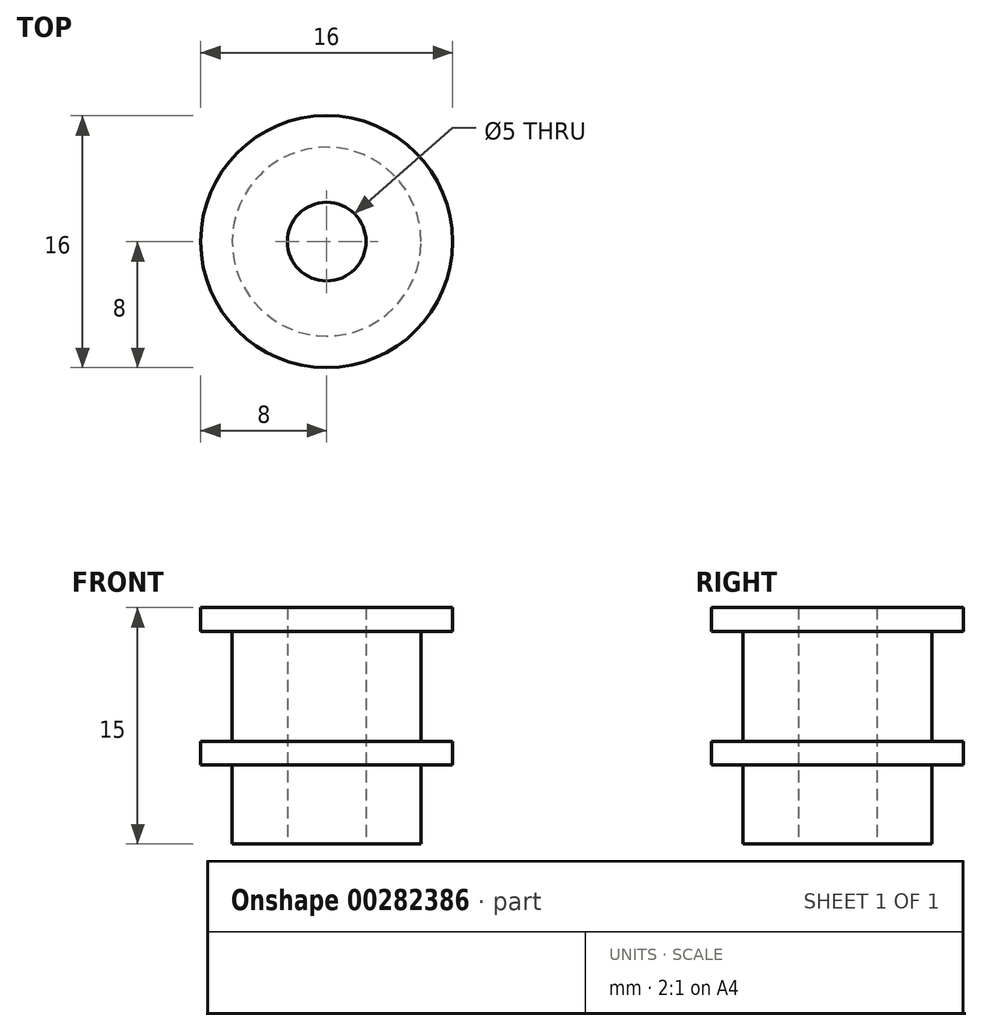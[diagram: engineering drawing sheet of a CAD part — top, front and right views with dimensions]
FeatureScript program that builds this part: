
annotation { "Feature Type Name" : "Feature", "Feature Type Description" : "" }
export const myFeature = defineFeature(function(context is Context, id is Id, definition is map)
    precondition{}
    {
        {
            var Q0;
            Q0=qCreatedBy(makeId("Front.planeOp"),FACE);
            var sketch = newSketch(context, id + "F0", { "sketchPlane" : qUnion([Q0])});
            skLineSegment(sketch, "E0", {"start": v(0, 0) * mm, "end": v(0, 15) * mm, "construction": true});
            skLineSegment(sketch, "E1", {"start": v(2.5, 0) * mm, "end": v(2.5, 15) * mm});
            skLineSegment(sketch, "E2", {"start": v(2.5, 15) * mm, "end": v(8, 15) * mm});
            skLineSegment(sketch, "E3", {"start": v(8, 15) * mm, "end": v(8, 13.5) * mm});
            skLineSegment(sketch, "E4", {"start": v(8, 13.5) * mm, "end": v(6, 13.5) * mm});
            skLineSegment(sketch, "E5", {"start": v(6, 13.5) * mm, "end": v(6, 6.5) * mm});
            skLineSegment(sketch, "E6", {"start": v(6, 6.5) * mm, "end": v(8, 6.5) * mm});
            skLineSegment(sketch, "E7", {"start": v(8, 6.5) * mm, "end": v(8, 5) * mm});
            skLineSegment(sketch, "E8", {"start": v(8, 5) * mm, "end": v(6, 5) * mm});
            skLineSegment(sketch, "E9", {"start": v(6, 5) * mm, "end": v(6, 0) * mm});
            skLineSegment(sketch, "E10", {"start": v(6, 0) * mm, "end": v(2.5, 0) * mm});
            skSolve(sketch);
        }
        {
            var Q0;
            Q0=qSketchRegion(id+"F0",true);
            var Q1;
            Q1=sQuery(id+"F0.wireOp",EDGE,"E0");
            revolve(context, id + "F1", {"entities" : qUnion([Q0]), "axis" : qUnion([Q1]), "revolveType" : RevolveType.FULL});
        }
    });
